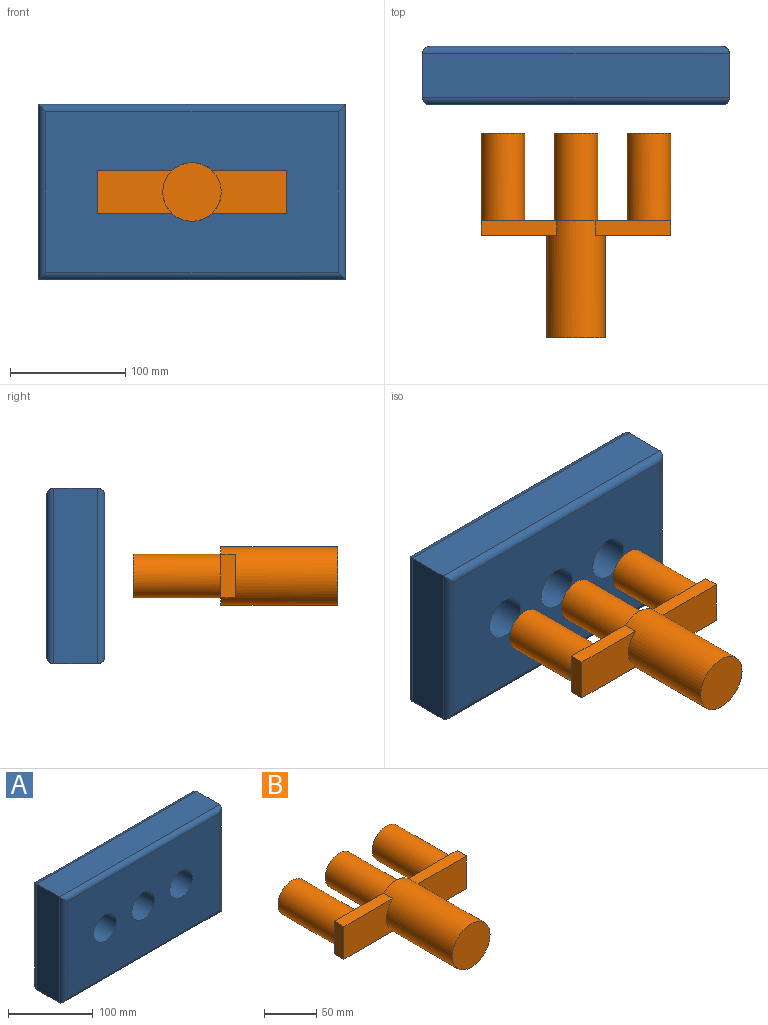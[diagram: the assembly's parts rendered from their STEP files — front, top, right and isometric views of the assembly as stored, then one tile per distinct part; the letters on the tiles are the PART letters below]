
ASSEMBLY  parts=2 mates=1
PART A: 17 faces, bbox 266.7x50.8x152.4 mm
  f0: plane 266.7x38.1mm, normal (0,0,1), area 10161.3mm2, adj f1,f6,f9,f13
  f1: plane 152.4x38.1mm, normal (-1,0,0), area 5806.4mm2, adj f0,f2,f10,f14
  f2: plane 266.7x38.1mm, normal (0,0,-1), area 10161.3mm2, adj f1,f6,f12,f16
  f3: cylinder r=19.04mm len=50.8mm, axis (0,1,0), area 6078.6mm2, adj f7,f8
  f4: cylinder r=19.05mm len=50.8mm, axis (0,1,0), area 6080.5mm2, adj f7,f8
  f5: cylinder r=19.05mm len=50.8mm, axis (0,1,0), area 6080.5mm2, adj f7,f8
  f6: plane 152.4x38.1mm, normal (1,0,0), area 5806.4mm2, adj f0,f2,f11,f15
  f7: plane 254x139.7mm, normal (0,-1,0), area 32064.2mm2, adj f3,f4,f5,f13,f14,f15,f16
  f8: plane 254x139.7mm, normal (0,1,0), area 32064.2mm2, adj f3,f4,f5,f9,f10,f11,f12
  f9: cylinder r=6.35mm len=266.7mm, axis (-1,0,0), area 2614.2mm2, adj f0,f8,f10,f11
  f10: cylinder r=6.35mm len=152.4mm, axis (0,0,-1), area 1474.1mm2, adj f1,f8,f9,f12
  f11: cylinder r=6.35mm len=152.4mm, axis (0,0,1), area 1474.1mm2, adj f6,f8,f9,f12
  f12: cylinder r=6.35mm len=266.7mm, axis (1,0,0), area 2614.2mm2, adj f2,f8,f10,f11
  f13: cylinder r=6.35mm len=266.7mm, axis (1,0,0), area 2614.2mm2, adj f0,f7,f14,f15
  f14: cylinder r=6.35mm len=152.4mm, axis (0,0,1), area 1474.1mm2, adj f1,f7,f13,f16
  f15: cylinder r=6.35mm len=152.4mm, axis (0,0,-1), area 1474.1mm2, adj f6,f7,f13,f16
  f16: cylinder r=6.35mm len=266.7mm, axis (-1,0,0), area 2614.2mm2, adj f2,f7,f14,f15
PART B: 21 faces, bbox 165.1x177.8x50.8 mm
  f0: plane 19.05x19.05mm, normal (0,1,0), area 77.9mm2, adj f7,f10,f19
  f1: plane 19.05x19.05mm, normal (0,1,0), area 77.9mm2, adj f7,f9,f19
  f2: plane 19.05x19.05mm, normal (0,1,0), area 77.9mm2, adj f12,f14,f17
  f3: plane 127x50.8mm, normal (0,1,0), area 2851mm2, adj f4,f9,f10,f12,f13,f15,f17,f19
  f4: cylinder r=25.4mm len=101.6mm, axis (0,1,0), area 15120.4mm2, adj f3,f5,f8,f9,f10,f11,f12,f13
  f5: plane 50.8x50.8mm, normal (0,-1,0), area 2026.8mm2, adj f4
  f6: plane 19.05x19.05mm, normal (0,1,0), area 77.9mm2, adj f13,f14,f17
  f7: plane 38.1x12.7mm, normal (-1,0,0), area 483.9mm2, adj f0,f1,f8,f9,f10
  f8: plane 65.75x38.1mm, normal (0,-1,0), area 2278mm2, adj f4,f7,f9,f10
  f9: plane 65.75x12.7mm, normal (0,0,-1), area 835mm2, adj f1,f3,f4,f7,f8
  f10: plane 65.75x12.7mm, normal (0,0,1), area 835mm2, adj f0,f3,f4,f7,f8
  f11: plane 65.75x38.1mm, normal (0,-1,0), area 2278mm2, adj f4,f12,f13,f14
  f12: plane 65.75x12.7mm, normal (0,0,1), area 835mm2, adj f2,f3,f4,f11,f14
  f13: plane 65.75x12.7mm, normal (0,0,-1), area 835mm2, adj f3,f4,f6,f11,f14
  f14: plane 38.1x12.7mm, normal (1,0,0), area 483.9mm2, adj f2,f6,f11,f12,f13
  f15: cylinder r=19.05mm len=76.2mm, axis (0,-1,0), area 9120.7mm2, adj f3,f16
  f16: plane 38.1x38.1mm, normal (0,1,0), area 1140.1mm2, adj f15
  f17: cylinder r=19.05mm len=76.2mm, axis (0,-1,0), area 9120.7mm2, adj f2,f3,f6,f18
  f18: plane 38.1x38.1mm, normal (0,1,0), area 1140.1mm2, adj f17
  f19: cylinder r=19.05mm len=76.2mm, axis (0,-1,0), area 9120.7mm2, adj f0,f1,f3,f20
  f20: plane 38.1x38.1mm, normal (0,1,0), area 1140.1mm2, adj f19
PLACE A rot(axis=(1,0,0),180deg) t=(-78.39,-294.18,6.34)mm
PLACE B t=(-78.39,-395.02,-24.39)mm
MATE slider A.f4 <-> B.f19  axis (0,1,0) through (-141.89,-243.38,-24.39)mm
